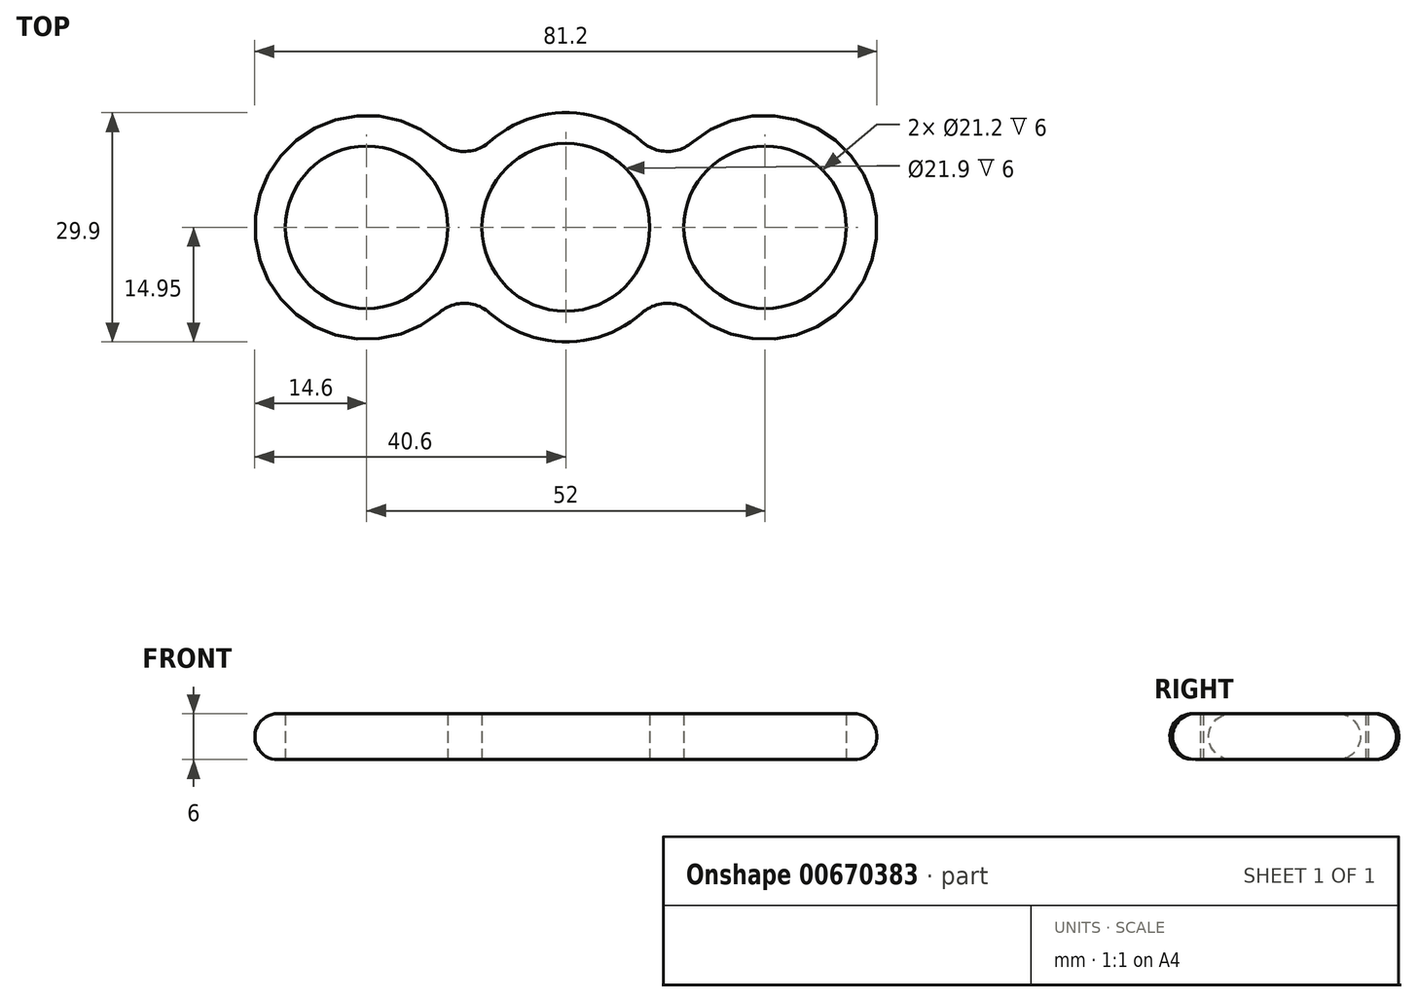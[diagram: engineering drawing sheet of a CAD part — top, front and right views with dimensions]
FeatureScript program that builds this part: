
annotation { "Feature Type Name" : "Feature", "Feature Type Description" : "" }
export const myFeature = defineFeature(function(context is Context, id is Id, definition is map)
    precondition{}
    {
        {
            var Q0;
            Q0=qCreatedBy(makeId("Top.planeOp"),FACE);
            var sketch = newSketch(context, id + "F0", { "sketchPlane" : qUnion([Q0])});
            skCircle(sketch, "E0", {"center": v(0, 0) * mm, "radius": 10.95 * mm});
            skLineSegment(sketch, "E1", {"start": v(0, 63.78) * mm, "end": v(0, -64.4) * mm, "construction": true});
            skLineSegment(sketch, "E2", {"start": v(-66.98, 0) * mm, "end": v(67.4, 0) * mm, "construction": true});
            skCircle(sketch, "E3", {"center": v(26, 0) * mm, "radius": 10.6 * mm});
            skCircle(sketch, "E4.MirrorC", {"center": v(-26, 0) * mm, "radius": 10.6 * mm});
            skCircle(sketch, "E5.0", {"center": v(-26, 0) * mm, "radius": 14.6 * mm});
            skCircle(sketch, "E6.0", {"center": v(26, 0) * mm, "radius": 14.6 * mm});
            skCircle(sketch, "E7.0", {"center": v(0, 0) * mm, "radius": 14.95 * mm});
            skSolve(sketch);
        }
        {
            var Q0;
            Q0 = qSketchRegion(id + "F0", true);
            extrude(context, id + "F1", {"entities" : qUnion([Q0]), "depth" : 6 * mm, "offsetDistance" : 25 * mm});
        }
        {
            var Q0;
            {var subQ0=sQuery(id+"F0.wireOp",EDGE,"E7.0");var subQ1=sQuery(id+"F0.wireOp",EDGE,"E5.0");Q0=makeQuery(id+"F1.opExtrude","SWEPT_EDGE",EDGE,{"disambiguationData":[OSD([subQ1,subQ0]),TDD([makeQuery(id+"F0.imprint","INTERSECT",VERTEX,{"disambiguationData":[OD(1.0)],"derivedFrom":[subQ1,subQ0]})])]});}
            var Q1;
            {var subQ0=sQuery(id+"F0.wireOp",EDGE,"E7.0");var subQ1=sQuery(id+"F0.wireOp",EDGE,"E6.0");Q1=makeQuery(id+"F1.opExtrude","SWEPT_EDGE",EDGE,{"disambiguationData":[OSD([subQ1,subQ0]),TDD([makeQuery(id+"F0.imprint","INTERSECT",VERTEX,{"disambiguationData":[OD(1.0)],"derivedFrom":[subQ1,subQ0]})])]});}
            var Q2;
            {var subQ0=sQuery(id+"F0.wireOp",EDGE,"E7.0");var subQ1=sQuery(id+"F0.wireOp",EDGE,"E6.0");Q2=makeQuery(id+"F1.opExtrude","SWEPT_EDGE",EDGE,{"disambiguationData":[OSD([subQ1,subQ0]),TDD([makeQuery(id+"F0.imprint","INTERSECT",VERTEX,{"disambiguationData":[OD(0.0)],"derivedFrom":[subQ1,subQ0]})])]});}
            var Q3;
            {var subQ0=sQuery(id+"F0.wireOp",EDGE,"E7.0");var subQ1=sQuery(id+"F0.wireOp",EDGE,"E5.0");Q3=makeQuery(id+"F1.opExtrude","SWEPT_EDGE",EDGE,{"disambiguationData":[OSD([subQ1,subQ0]),TDD([makeQuery(id+"F0.imprint","INTERSECT",VERTEX,{"disambiguationData":[OD(0.0)],"derivedFrom":[subQ1,subQ0]})])]});}
            fillet(context, id + "F2", {"entities" : qUnion([Q0, Q1, Q2, Q3]), "radius" : 5 * mm, "tangentPropagation" : true, "allowEdgeOverflow" : false});
        }
        {
            var Q0;
            Q0=makeQuery(id+"F1.opExtrude","CAP_EDGE",EDGE,{"disambiguationData":[OSD([sQuery(id+"F0.wireOp",EDGE,"E5.0")])],"isStart":false});
            var Q1;
            {var subQ0=sQuery(id+"F0.wireOp",EDGE,"E7.0");Q1=makeQuery(id+"F1.opExtrude","CAP_EDGE",EDGE,{"disambiguationData":[OSD([subQ0]),TDD([makeQuery(id+"F0.imprint","IMPRINT",EDGE,{"disambiguationData":[TD([[makeQuery(id+"F0.imprint","INTERSECT",VERTEX,{"disambiguationData":[OD(1.0)],"derivedFrom":[sQuery(id+"F0.wireOp",EDGE,"E5.0"),subQ0]}),-1.0]])],"derivedFrom":subQ0})])],"isStart":true});}
            fillet(context, id + "F3", {"entities" : qUnion([Q0, Q1]), "radius" : 3 * mm, "tangentPropagation" : true, "allowEdgeOverflow" : false});
        }
    });
